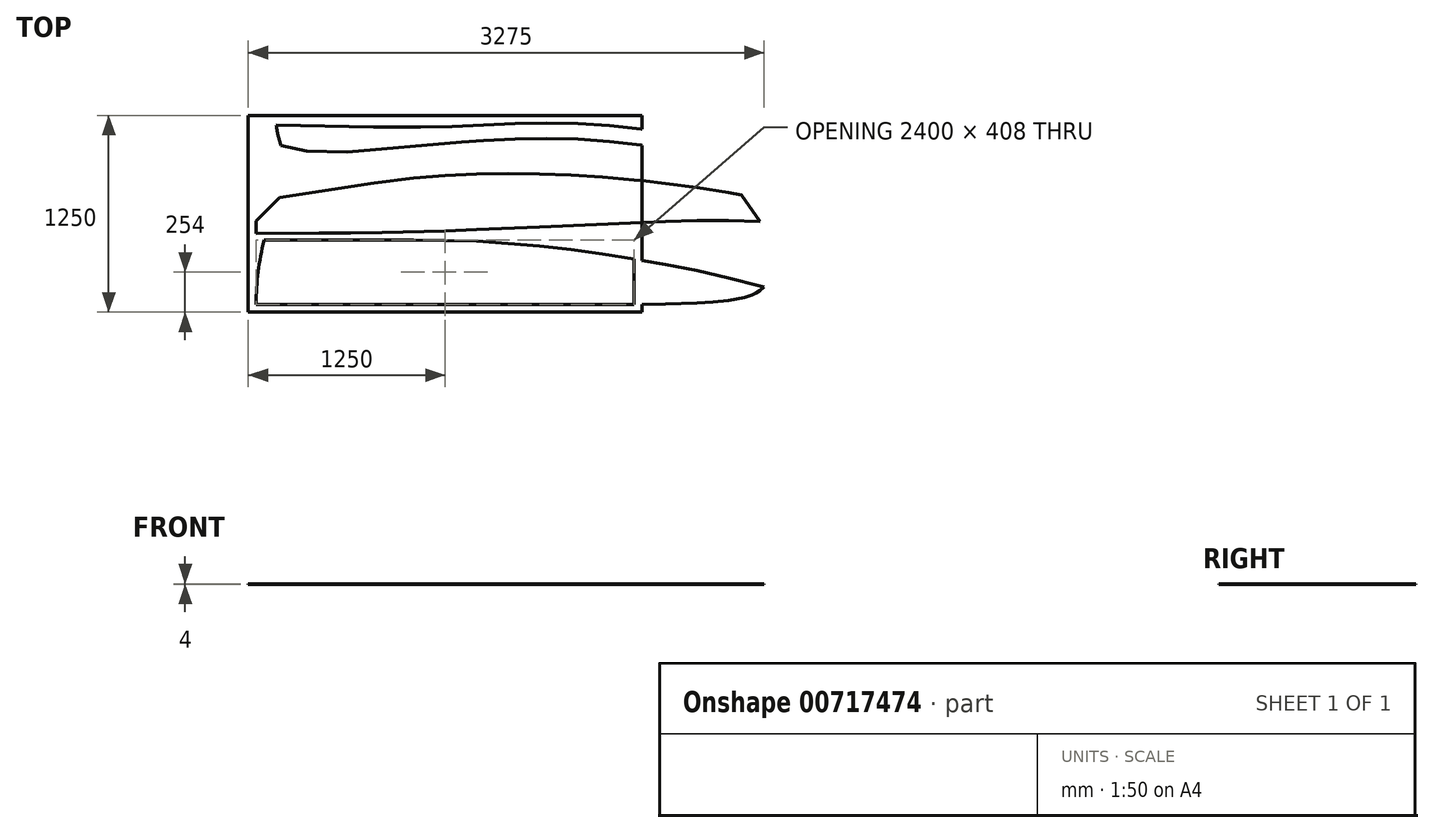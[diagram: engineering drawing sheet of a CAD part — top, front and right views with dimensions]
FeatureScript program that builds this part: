
annotation { "Feature Type Name" : "Feature", "Feature Type Description" : "" }
export const myFeature = defineFeature(function(context is Context, id is Id, definition is map)
    precondition{}
    {
        {
            var Q0;
            Q0=qCreatedBy(makeId("Top.planeOp"),FACE);
            var sketch = newSketch(context, id + "F0", { "sketchPlane" : qUnion([Q0])});
            skLineSegment(sketch, "E0", {"start": v(2500, 0) * mm, "end": v(2500, 1250) * mm});
            skLineSegment(sketch, "E1", {"start": v(2500, 1250) * mm, "end": v(0, 1250) * mm});
            skLineSegment(sketch, "E2", {"start": v(0, 1250) * mm, "end": v(0, 0) * mm});
            skLineSegment(sketch, "E3.2.0.0", {"start": v(0, 0) * mm, "end": v(2500, 0) * mm});
            skLineSegment(sketch, "E4", {"start": v(1625, 126) * mm, "end": v(1775, 126) * mm});
            skArc(sketch, "E5", {"start": v(50, 50) * mm, "mid": v(62.55, 255.53) * mm, "end": v(100, 458) * mm});
            skLineSegment(sketch, "E6", {"start": v(50, 50) * mm, "end": v(2450, 50) * mm});
            skLineSegment(sketch, "E7", {"start": v(100, 458) * mm, "end": v(1050, 458) * mm});
            skLineSegment(sketch, "E8", {"start": v(1050, 458) * mm, "end": v(1050, 50) * mm});
            skLineSegment(sketch, "E9.1.0.0", {"start": v(1250, 457) * mm, "end": v(1250, 50) * mm});
            skLineSegment(sketch, "E9.2.0.0", {"start": v(1450, 451) * mm, "end": v(1450, 50) * mm});
            skLineSegment(sketch, "E9.3.0.0", {"start": v(1650, 438) * mm, "end": v(1650, 50) * mm});
            skLineSegment(sketch, "E9.4.0.0", {"start": v(1850, 420) * mm, "end": v(1850, 50) * mm});
            skLineSegment(sketch, "E9.5.0.0", {"start": v(2050, 397) * mm, "end": v(2050, 50) * mm});
            skLineSegment(sketch, "E9.6.0.0", {"start": v(2250, 370) * mm, "end": v(2250, 50) * mm});
            skLineSegment(sketch, "E9.7.0.0", {"start": v(2450, 338) * mm, "end": v(2450, 50) * mm});
            skLineSegment(sketch, "E9.8.0.0", {"start": v(2650, 303) * mm, "end": v(2650, 50) * mm});
            skLineSegment(sketch, "E9.9.0.0", {"start": v(2850, 264) * mm, "end": v(2850, 50) * mm});
            skLineSegment(sketch, "E9.10.0.0", {"start": v(3050, 219) * mm, "end": v(3050, 50) * mm});
            skLineSegment(sketch, "E9.11.0.0", {"start": v(3250, 137) * mm, "end": v(3250, 50) * mm});
            skLineSegment(sketch, "E9.direction1", {"start": v(1050, 50) * mm, "end": v(1250, 50) * mm, "construction": true});
            skLineSegment(sketch, "E10", {"start": v(3275, 159) * mm, "end": v(3250, 166) * mm});
            skLineSegment(sketch, "E11", {"start": v(3050, 219) * mm, "end": v(2850, 264) * mm});
            skLineSegment(sketch, "E12", {"start": v(2650, 303) * mm, "end": v(2850, 264) * mm});
            skLineSegment(sketch, "E13", {"start": v(3050, 219) * mm, "end": v(3250, 166) * mm});
            skLineSegment(sketch, "E14", {"start": v(1050, 458) * mm, "end": v(1250, 457) * mm});
            skLineSegment(sketch, "E15", {"start": v(1450, 451) * mm, "end": v(1250, 457) * mm});
            skLineSegment(sketch, "E16", {"start": v(1450, 451) * mm, "end": v(1650, 438) * mm});
            skLineSegment(sketch, "E17", {"start": v(1650, 438) * mm, "end": v(1850, 420) * mm});
            skLineSegment(sketch, "E18", {"start": v(1850, 420) * mm, "end": v(2050, 397) * mm});
            skLineSegment(sketch, "E19", {"start": v(2050, 397) * mm, "end": v(2250, 370) * mm});
            skLineSegment(sketch, "E20", {"start": v(2250, 370) * mm, "end": v(2450, 338) * mm});
            skLineSegment(sketch, "E21", {"start": v(2450, 338) * mm, "end": v(2650, 303) * mm});
            skLineSegment(sketch, "E22", {"start": v(2650, 52) * mm, "end": v(2450, 50) * mm});
            skLineSegment(sketch, "E23", {"start": v(2650, 52) * mm, "end": v(2850, 58) * mm});
            skLineSegment(sketch, "E24", {"start": v(2950, 50) * mm, "end": v(2950, 64) * mm});
            skLineSegment(sketch, "E25", {"start": v(2950, 64) * mm, "end": v(3050, 75) * mm});
            skLineSegment(sketch, "E26", {"start": v(2850, 58) * mm, "end": v(2950, 64) * mm});
            skLineSegment(sketch, "E27", {"start": v(3150, 50) * mm, "end": v(3150, 94) * mm});
            skLineSegment(sketch, "E28", {"start": v(3100, 83) * mm, "end": v(3100, 50) * mm});
            skLineSegment(sketch, "E29", {"start": v(3200, 111) * mm, "end": v(3200, 50) * mm});
            skLineSegment(sketch, "E30", {"start": v(3100, 83) * mm, "end": v(3150, 94) * mm});
            skLineSegment(sketch, "E31", {"start": v(3050, 75) * mm, "end": v(3100, 83) * mm});
            skLineSegment(sketch, "E32", {"start": v(3150, 94) * mm, "end": v(3200, 111) * mm});
            skLineSegment(sketch, "E33", {"start": v(3225, 50) * mm, "end": v(3225, 122) * mm});
            skLineSegment(sketch, "E34", {"start": v(3200, 111) * mm, "end": v(3225, 122) * mm});
            skLineSegment(sketch, "E35", {"start": v(3225, 122) * mm, "end": v(3250, 137) * mm});
            skLineSegment(sketch, "E36", {"start": v(3250, 137) * mm, "end": v(3275, 159) * mm});
            skLineSegment(sketch, "E37", {"start": v(50, 500) * mm, "end": v(50, 580) * mm});
            skLineSegment(sketch, "E38", {"start": v(200, 730) * mm, "end": v(50, 580) * mm});
            skLineSegment(sketch, "E39", {"start": v(200, 730) * mm, "end": v(800, 821) * mm});
            skLineSegment(sketch, "E40", {"start": v(3133, 746) * mm, "end": v(3251, 577) * mm});
            skLineSegment(sketch, "E41", {"start": v(800, 821) * mm, "end": v(1050, 852) * mm});
            skLineSegment(sketch, "E42", {"start": v(1250, 868) * mm, "end": v(1050, 852) * mm});
            skLineSegment(sketch, "E43", {"start": v(1250, 868) * mm, "end": v(1450, 877) * mm});
            skLineSegment(sketch, "E44", {"start": v(1450, 877) * mm, "end": v(1650, 880) * mm});
            skLineSegment(sketch, "E45", {"start": v(50, 500) * mm, "end": v(4321.2, 500) * mm, "construction": true});
            skLineSegment(sketch, "E46", {"start": v(650, 504) * mm, "end": v(850, 507) * mm});
            skLineSegment(sketch, "E47", {"start": v(850, 507) * mm, "end": v(1050, 512) * mm});
            skLineSegment(sketch, "E48", {"start": v(650, 504) * mm, "end": v(450, 502) * mm});
            skLineSegment(sketch, "E49", {"start": v(450, 502) * mm, "end": v(50, 500) * mm});
            skLineSegment(sketch, "E50", {"start": v(1050, 512) * mm, "end": v(1250, 517) * mm});
            skLineSegment(sketch, "E51", {"start": v(1450, 524) * mm, "end": v(1250, 517) * mm});
            skLineSegment(sketch, "E52", {"start": v(1450, 524) * mm, "end": v(1650, 532) * mm});
            skLineSegment(sketch, "E53", {"start": v(1650, 532) * mm, "end": v(1850, 540) * mm});
            skLineSegment(sketch, "E54", {"start": v(1850, 540) * mm, "end": v(2050, 549) * mm});
            skLineSegment(sketch, "E55", {"start": v(2050, 549) * mm, "end": v(2250, 558) * mm});
            skLineSegment(sketch, "E56", {"start": v(2250, 558) * mm, "end": v(2450, 567) * mm});
            skLineSegment(sketch, "E57", {"start": v(2450, 567) * mm, "end": v(2650, 576) * mm});
            skLineSegment(sketch, "E58", {"start": v(2650, 576) * mm, "end": v(2850, 582) * mm});
            skLineSegment(sketch, "E59", {"start": v(2850, 582) * mm, "end": v(3050, 583) * mm});
            skLineSegment(sketch, "E60", {"start": v(1650, 880) * mm, "end": v(1850, 878) * mm});
            skLineSegment(sketch, "E61", {"start": v(1850, 878) * mm, "end": v(2050, 870) * mm});
            skLineSegment(sketch, "E62", {"start": v(2050, 870) * mm, "end": v(2250, 858) * mm});
            skLineSegment(sketch, "E63", {"start": v(2250, 858) * mm, "end": v(2450, 841) * mm});
            skLineSegment(sketch, "E64", {"start": v(2450, 841) * mm, "end": v(2650, 819) * mm});
            skLineSegment(sketch, "E65", {"start": v(2650, 819) * mm, "end": v(2850, 792) * mm});
            skLineSegment(sketch, "E66", {"start": v(2850, 792) * mm, "end": v(3050, 761) * mm});
            skLineSegment(sketch, "E67", {"start": v(3050, 761) * mm, "end": v(3133, 746) * mm});
            skLineSegment(sketch, "E68", {"start": v(3050, 583) * mm, "end": v(3251, 577) * mm});
            skLineSegment(sketch, "E69", {"start": v(208.17, 1058) * mm, "end": v(370.17, 1025) * mm});
            skLineSegment(sketch, "E70", {"start": v(3028.17, 948) * mm, "end": v(3127.17, 965) * mm});
            skLineSegment(sketch, "E71", {"start": v(3112.17, 1036) * mm, "end": v(3127.17, 965) * mm});
            skLineSegment(sketch, "E72", {"start": v(177.17, 1188) * mm, "end": v(797.17, 1177) * mm});
            skLineSegment(sketch, "E73", {"start": v(628.17, 1018) * mm, "end": v(1355.17, 1080) * mm});
            skLineSegment(sketch, "E74", {"start": v(370.17, 1025) * mm, "end": v(628.17, 1018) * mm});
            skLineSegment(sketch, "E75", {"start": v(396.17, 746) * mm, "end": v(95.17, 746) * mm});
            skLineSegment(sketch, "E76", {"start": v(396.17, 746) * mm, "end": v(509.17, 746) * mm});
            skPoint(sketch, "E77.orphan", {"position": v(2895.17, 746) * mm});
            skPoint(sketch, "E78.orphan", {"position": v(2695.17, 746) * mm});
            skPoint(sketch, "E79.orphan", {"position": v(2495.17, 746) * mm});
            skPoint(sketch, "E80.orphan", {"position": v(2295.17, 746) * mm});
            skPoint(sketch, "E81.orphan", {"position": v(2095.17, 746) * mm});
            skPoint(sketch, "E82.orphan", {"position": v(1495.17, 746) * mm});
            skPoint(sketch, "E83.orphan", {"position": v(1695.17, 746) * mm});
            skPoint(sketch, "E84.orphan", {"position": v(1895.17, 746) * mm});
            skLineSegment(sketch, "E85", {"start": v(1355.17, 1080) * mm, "end": v(1495.17, 1090) * mm});
            skLineSegment(sketch, "E86", {"start": v(1495.17, 1090) * mm, "end": v(1695.17, 1101) * mm});
            skLineSegment(sketch, "E87", {"start": v(1695.17, 1101) * mm, "end": v(1895.17, 1104) * mm});
            skLineSegment(sketch, "E88", {"start": v(1895.17, 1104) * mm, "end": v(2095.17, 1099) * mm});
            skLineSegment(sketch, "E89", {"start": v(2095.17, 1099) * mm, "end": v(2295.17, 1085) * mm});
            skLineSegment(sketch, "E90", {"start": v(2295.17, 1085) * mm, "end": v(2495.17, 1061) * mm});
            skLineSegment(sketch, "E91", {"start": v(2495.17, 1061) * mm, "end": v(2695.17, 1028) * mm});
            skLineSegment(sketch, "E92", {"start": v(2695.17, 1028) * mm, "end": v(2895.17, 984) * mm});
            skLineSegment(sketch, "E93", {"start": v(2895.17, 984) * mm, "end": v(3028.17, 948) * mm});
            skLineSegment(sketch, "E94", {"start": v(3112.17, 1036) * mm, "end": v(2895.17, 1091) * mm});
            skLineSegment(sketch, "E95", {"start": v(2895.17, 1091) * mm, "end": v(2695.17, 1132) * mm});
            skLineSegment(sketch, "E96", {"start": v(2695.17, 1132) * mm, "end": v(2495.17, 1163) * mm});
            skLineSegment(sketch, "E97", {"start": v(2495.17, 1163) * mm, "end": v(2295.17, 1185) * mm});
            skLineSegment(sketch, "E98", {"start": v(2295.17, 1185) * mm, "end": v(2095.17, 1198) * mm});
            skLineSegment(sketch, "E99", {"start": v(2095.17, 1198) * mm, "end": v(1895.17, 1203) * mm});
            skLineSegment(sketch, "E100", {"start": v(1895.17, 1203) * mm, "end": v(1695.17, 1200) * mm});
            skLineSegment(sketch, "E101", {"start": v(1695.17, 1200) * mm, "end": v(1495.17, 1190) * mm});
            skLineSegment(sketch, "E102", {"start": v(797.17, 1177) * mm, "end": v(1095.17, 1177) * mm});
            skLineSegment(sketch, "E103", {"start": v(1095.17, 1177) * mm, "end": v(1295.17, 1181) * mm});
            skLineSegment(sketch, "E104", {"start": v(1295.17, 1181) * mm, "end": v(1495.17, 1190) * mm});
            skFitSpline(sketch, "E105", {"points": [v(177.17, 1188) * mm, v(208.17, 1058) * mm], "startDerivative": vector(17.06, -131.2) * mm, "endDerivative": vector(41.17, -128.02) * mm});
            skSolve(sketch);
        }
        {
            var Q0;
            Q0=makeQuery(id+"F0.imprint","IMPRINT",FACE,{"disambiguationData":[TD([[makeQuery(id+"F0.imprint","IMPRINT",EDGE,{"derivedFrom":sQuery(id+"F0.wireOp",EDGE,"E10")}),1.0]])]});
            var Q1;
            {var subQ0=sQuery(id+"F0.wireOp",EDGE,"E22");var subQ1=sQuery(id+"F0.wireOp",EDGE,"E0");var subQ2=makeQuery(id+"F0.imprint","INTERSECT",VERTEX,{"derivedFrom":[subQ1,subQ0]});Q1=makeQuery(id+"F0.imprint","IMPRINT",FACE,{"disambiguationData":[TD([[makeQuery(id+"F0.imprint","IMPRINT",EDGE,{"disambiguationData":[TD([[subQ2,-1.0]])],"derivedFrom":subQ1}),-1.0]])]});}
            var Q2;
            {var subQ0=sQuery(id+"F0.wireOp",EDGE,"E12");Q2=makeQuery(id+"F0.imprint","IMPRINT",FACE,{"disambiguationData":[TD([[makeQuery(id+"F0.imprint","IMPRINT",EDGE,{"derivedFrom":subQ0}),-1.0]])]});}
            var Q3;
            {var subQ1=sQuery(id+"F0.wireOp",EDGE,"E11");Q3=makeQuery(id+"F0.imprint","IMPRINT",FACE,{"disambiguationData":[TD([[makeQuery(id+"F0.imprint","IMPRINT",EDGE,{"derivedFrom":subQ1}),1.0]])]});}
            var Q4;
            {var subQ5=sQuery(id+"F0.wireOp",EDGE,"E9.7.0.0");Q4=makeQuery(id+"F0.imprint","IMPRINT",FACE,{"disambiguationData":[TD([[makeQuery(id+"F0.imprint","IMPRINT",EDGE,{"derivedFrom":subQ5}),1.0]])]});}
            var Q5;
            {var subQ17=sQuery(id+"F0.wireOp",EDGE,"E1");Q5=makeQuery(id+"F0.imprint","IMPRINT",FACE,{"disambiguationData":[TD([[makeQuery(id+"F0.imprint","IMPRINT",EDGE,{"derivedFrom":subQ17}),1.0]])]});}
            var Q6;
            Q6=makeQuery(id+"F0.imprint","IMPRINT",FACE,{"disambiguationData":[TD([[makeQuery(id+"F0.imprint","IMPRINT",EDGE,{"derivedFrom":sQuery(id+"F0.wireOp",EDGE,"E40")}),-1.0]])]});
            extrude(context, id + "F1", {"entities" : qUnion([Q0, Q1, Q2, Q3, Q4, Q5, Q6]), "depth" : 4 * mm, "offsetDistance" : 25 * mm});
        }
    });
